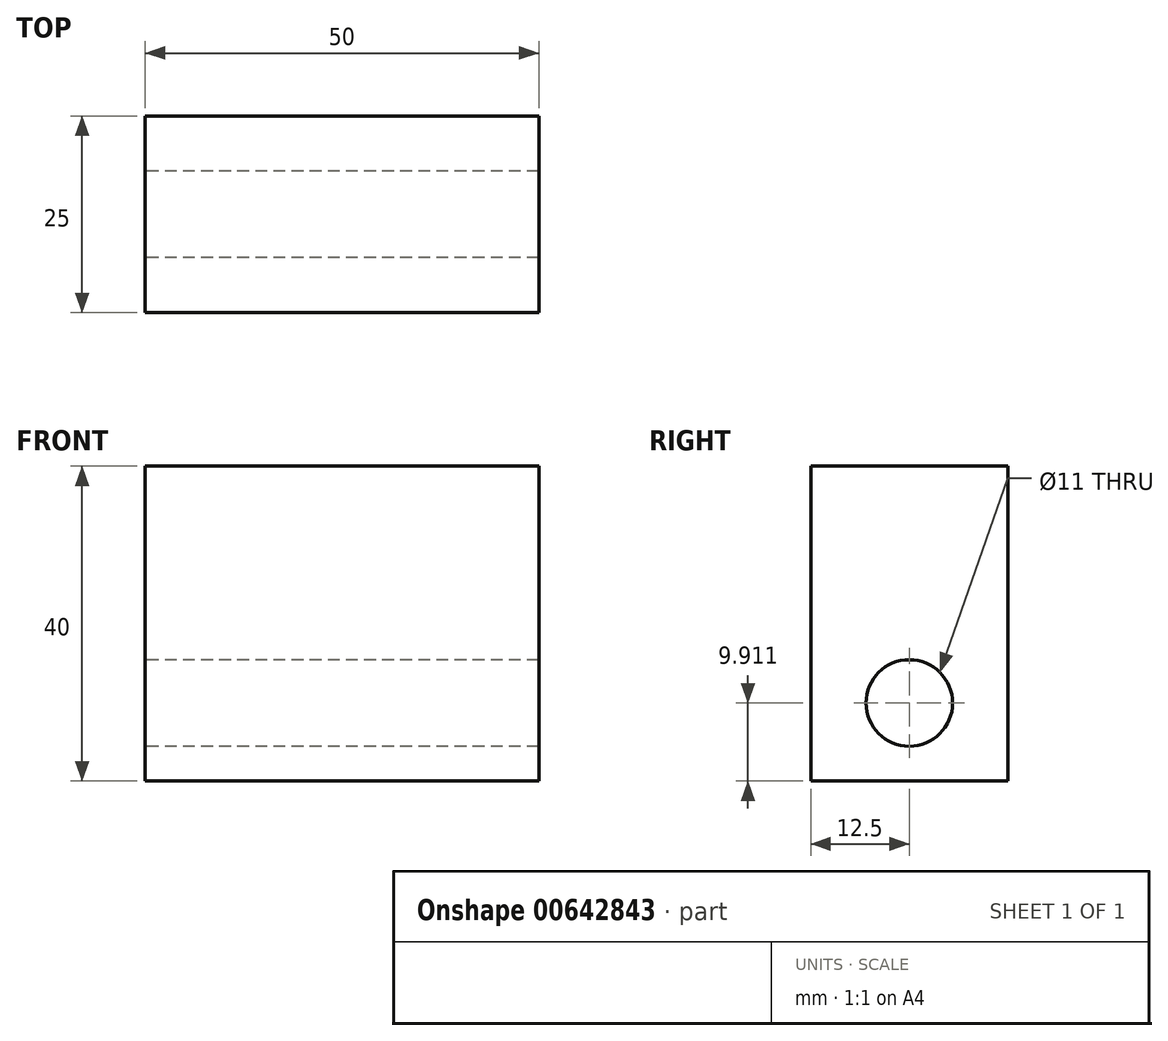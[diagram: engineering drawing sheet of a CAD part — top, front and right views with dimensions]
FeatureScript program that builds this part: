
annotation { "Feature Type Name" : "Feature", "Feature Type Description" : "" }
export const myFeature = defineFeature(function(context is Context, id is Id, definition is map)
    precondition{}
    {
        {
            var Q0;
            Q0=qCreatedBy(makeId("Front.planeOp"),FACE);
            var sketch = newSketch(context, id + "F0", { "sketchPlane" : qUnion([Q0])});
            skLineSegment(sketch, "E0.bottom", {"start": v(0, 0) * mm, "end": v(50, 0) * mm});
            skLineSegment(sketch, "E0.top", {"start": v(0, 40) * mm, "end": v(50, 40) * mm});
            skLineSegment(sketch, "E0.left", {"start": v(0, 0) * mm, "end": v(0, 40) * mm});
            skLineSegment(sketch, "E0.right", {"start": v(50, 0) * mm, "end": v(50, 40) * mm});
            skSolve(sketch);
        }
        {
            var Q0;
            Q0 = qSketchRegion(id + "F0", true);
            extrude(context, id + "F1", {"entities" : qUnion([Q0]), "depth" : 25 * mm, "offsetDistance" : 25 * mm});
        }
        {
            var Q0;
            Q0=makeQuery(id+"F1.opExtrude","SWEPT_FACE",FACE,{"disambiguationData":[OSD([sQuery(id+"F0.wireOp",EDGE,"E0.left")])]});
            var sketch = newSketch(context, id + "F2", { "sketchPlane" : qUnion([Q0])});
            skLineSegment(sketch, "E1", {"start": v(12.5, 0) * mm, "end": v(12.5, 40) * mm, "construction": true});
            skCircle(sketch, "E2", {"center": v(12.5, 9.91) * mm, "radius": 5.5 * mm});
            skSolve(sketch);
        }
        {
            var Q0;
            Q0=makeQuery(id+"F2.imprint","IMPRINT",FACE,{"disambiguationData":[TD([[makeQuery(id+"F2.imprint","IMPRINT",EDGE,{"derivedFrom":sQuery(id+"F2.wireOp",EDGE,"E2")}),1.0]])]});
            var Q1;
            Q1=sQuery(id+"F2.wireOp",EDGE,"E2");
            extrude(context, id + "F3", {"entities" : qUnion([Q0]), "operationType" : NewBodyOperationType.REMOVE, "surfaceEntities" : qUnion([Q1]), "oppositeDirection" : true, "depth" : 100 * mm, "offsetDistance" : 25 * mm});
        }
    });
